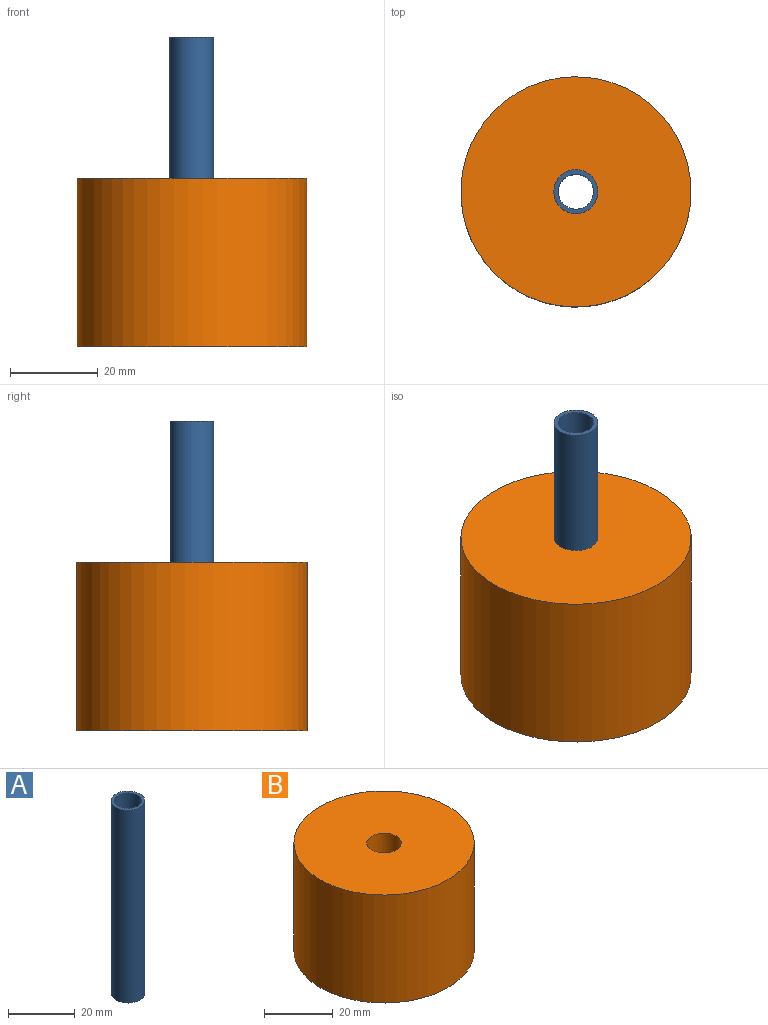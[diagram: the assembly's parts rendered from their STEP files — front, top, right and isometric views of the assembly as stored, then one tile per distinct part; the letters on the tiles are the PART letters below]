
ASSEMBLY  parts=2 mates=1
PART A: 4 faces, bbox 10x10x70.5 mm
  f0: cylinder r=5mm len=70.5mm, axis (0,0,-1), area 2214.8mm2, adj f1,f3
  f1: plane 10x10mm, normal (0,0,1), area 28.3mm2, adj f0,f2
  f2: cylinder r=4mm len=70.5mm, axis (0,0,-1), area 1771.9mm2, adj f1,f3
  f3: plane 10x10mm, normal (0,0,-1), area 28.3mm2, adj f0,f2
PART B: 4 faces, bbox 52.4x52.4x38.4 mm
  f0: cylinder r=26.2mm len=52.4mm, axis (0,0,-1), area 6320.8mm2, adj f1,f2
  f1: plane 52.4x52.4mm, normal (0,0,1), area 2077.5mm2, adj f0,f3
  f2: plane 52.4x52.4mm, normal (0,0,-1), area 2077.5mm2, adj f0,f3
  f3: cylinder r=5mm len=38.4mm, axis (0,0,-1), area 1206.4mm2, adj f1,f2
PLACE A t=(13.84,29.5,-165.59)mm
PLACE B t=(13.84,29.5,13.31)mm fixed
MATE slider B.f0 <-> A.f0  axis (0,0,-1) through (13.84,29.5,-95.59)mm
